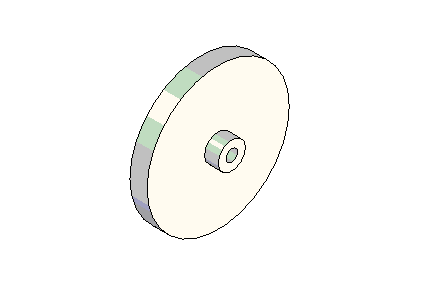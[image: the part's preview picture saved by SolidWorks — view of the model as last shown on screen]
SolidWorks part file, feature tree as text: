
SOLIDWORKS PART (.sldprt)
format: sldprt  version: not decoded by parser v0  size: 109,568 bytes
history: native  units: mm
features: sketch x3, extrude x2, cut_extrude x1 (+11 scaffold rows collapsed)
feature tree (17):
  scaffold x11  (default folders/planes/origin — collapsed)
  sketch  "Sketch1"  dims[D1=22.225mm]
  extrude  "Extrude1"  Depth=11.1125mm
  sketch  "Sketch2"  dims[D1=115.57mm]
  extrude  "Extrude2"  Depth=13.97mm
  sketch  "Sketch5"  dims[D1=9.525mm]
  cut_extrude  "Cut-Extrude1"  [1 undecoded]
decode coverage: 5 of 6 modeling features carry decoded parameters
note: 1 parameter value undecoded
note: suppression state not decoded; provenance and decode notes live in map.json
